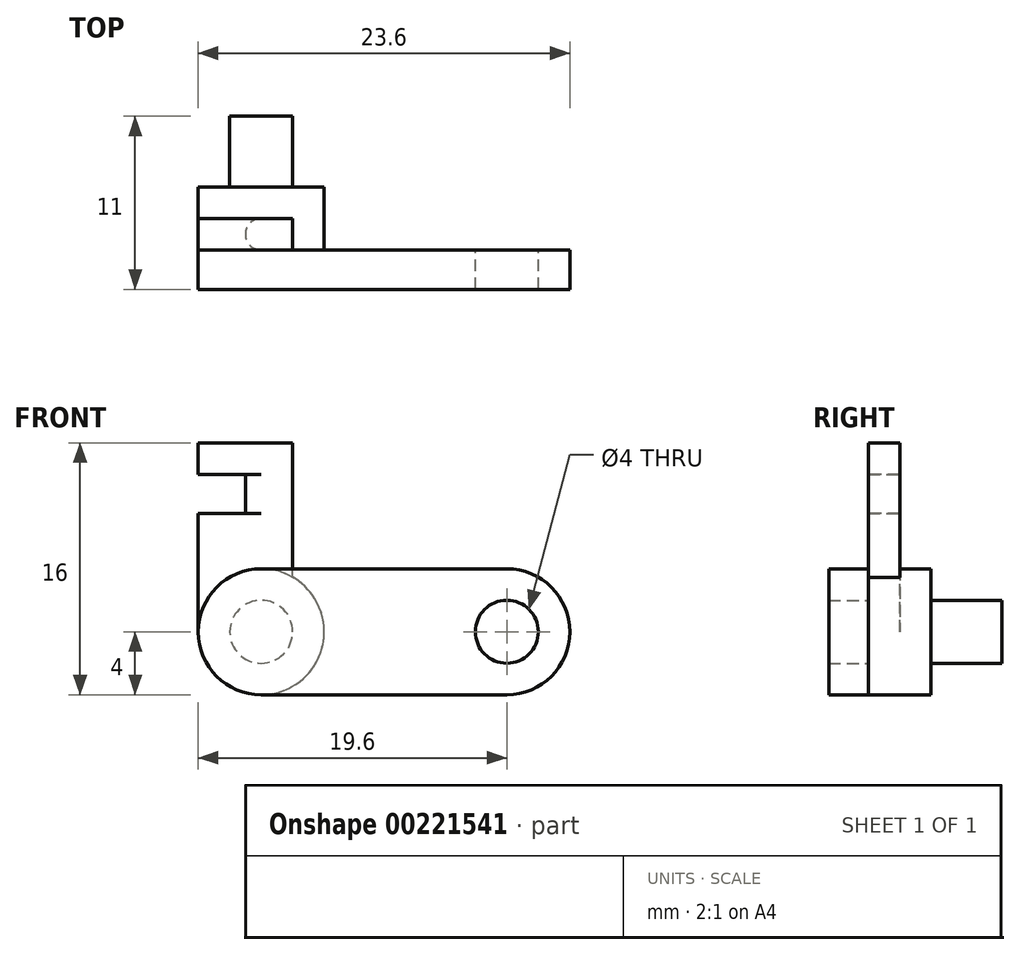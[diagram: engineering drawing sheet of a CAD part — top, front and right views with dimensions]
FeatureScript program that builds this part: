
annotation { "Feature Type Name" : "Feature", "Feature Type Description" : "" }
export const myFeature = defineFeature(function(context is Context, id is Id, definition is map)
    precondition{}
    {
        {
            var Q0;
            Q0=qCreatedBy(makeId("Front.planeOp"),FACE);
            var sketch = newSketch(context, id + "F0", { "sketchPlane" : qUnion([Q0])});
            skCircle(sketch, "E0", {"center": v(0, 0) * mm, "radius": 2 * mm});
            skCircle(sketch, "E1", {"center": v(0, 0) * mm, "radius": 4 * mm});
            skLineSegment(sketch, "E2", {"start": v(0, 4) * mm, "end": v(15.6, 4) * mm});
            skLineSegment(sketch, "E3", {"start": v(0, -4) * mm, "end": v(15.6, -4) * mm});
            skArc(sketch, "E4", {"start": v(15.6, 4) * mm, "mid": v(19.6, 0) * mm, "end": v(15.6, -4) * mm});
            skCircle(sketch, "E5", {"center": v(15.6, 0) * mm, "radius": 2 * mm});
            skLineSegment(sketch, "E6.bottom", {"start": v(2, 0) * mm, "end": v(-4, 0) * mm});
            skLineSegment(sketch, "E6.top", {"start": v(2, 12) * mm, "end": v(-4, 12) * mm});
            skLineSegment(sketch, "E6.left", {"start": v(2, 0) * mm, "end": v(2, 12) * mm});
            skLineSegment(sketch, "E6.right", {"start": v(-4, 0) * mm, "end": v(-4, 12) * mm});
            skLineSegment(sketch, "E7.bottom", {"start": v(-4, 10) * mm, "end": v(-1, 10) * mm});
            skLineSegment(sketch, "E7.top", {"start": v(-4, 7.5) * mm, "end": v(-1, 7.5) * mm});
            skLineSegment(sketch, "E7.left", {"start": v(-4, 10) * mm, "end": v(-4, 7.5) * mm});
            skLineSegment(sketch, "E7.right", {"start": v(-1, 10) * mm, "end": v(-1, 7.5) * mm});
            skSolve(sketch);
        }
        {
            var Q0;
            {var subQ1=sQuery(id+"F0.wireOp",EDGE,"E1");var subQ5=makeQuery(id+"F0.imprint","INTERSECT",VERTEX,{"derivedFrom":[subQ1,sQuery(id+"F0.wireOp",EDGE,"E3")]});Q0=makeQuery(id+"F0.imprint","IMPRINT",FACE,{"disambiguationData":[TD([[makeQuery(id+"F0.imprint","IMPRINT",EDGE,{"disambiguationData":[TD([[subQ5,-1.0]])],"derivedFrom":subQ1}),1.0]])]});}
            var Q1;
            {var subQ0=sQuery(id+"F0.wireOp",EDGE,"E2");var subQ1=sQuery(id+"F0.wireOp",EDGE,"E1");var subQ2=makeQuery(id+"F0.imprint","INTERSECT",VERTEX,{"derivedFrom":[subQ1,subQ0]});Q1=makeQuery(id+"F0.imprint","IMPRINT",FACE,{"disambiguationData":[TD([[makeQuery(id+"F0.imprint","IMPRINT",EDGE,{"disambiguationData":[TD([[subQ2,1.0]])],"derivedFrom":subQ1}),-1.0]])]});}
            var Q2;
            {var subQ1=sQuery(id+"F0.wireOp",EDGE,"E3");Q2=makeQuery(id+"F0.imprint","IMPRINT",FACE,{"disambiguationData":[TD([[makeQuery(id+"F0.imprint","IMPRINT",EDGE,{"derivedFrom":subQ1}),1.0]])]});}
            var Q3;
            {var subQ1=sQuery(id+"F0.wireOp",EDGE,"E1");var subQ5=makeQuery(id+"F0.imprint","INTERSECT",VERTEX,{"derivedFrom":[subQ1,sQuery(id+"F0.wireOp",EDGE,"E2")]});Q3=makeQuery(id+"F0.imprint","IMPRINT",FACE,{"disambiguationData":[TD([[makeQuery(id+"F0.imprint","IMPRINT",EDGE,{"disambiguationData":[TD([[subQ5,1.0]])],"derivedFrom":subQ1}),1.0]])]});}
            var Q4;
            {var subQ0=sQuery(id+"F0.wireOp",EDGE,"E6.bottom");var subQ1=sQuery(id+"F0.wireOp",EDGE,"E0");var subQ3=makeQuery(id+"F0.imprint","INTERSECT",VERTEX,{"derivedFrom":[subQ1,subQ0]});Q4=makeQuery(id+"F0.imprint","IMPRINT",FACE,{"disambiguationData":[TD([[makeQuery(id+"F0.imprint","IMPRINT",EDGE,{"disambiguationData":[TD([[subQ3,1.0]])],"derivedFrom":subQ1}),1.0]])]});}
            var Q5;
            {var subQ0=sQuery(id+"F0.wireOp",EDGE,"E6.bottom");var subQ1=sQuery(id+"F0.wireOp",EDGE,"E0");var subQ3=makeQuery(id+"F0.imprint","INTERSECT",VERTEX,{"derivedFrom":[subQ1,subQ0]});Q5=makeQuery(id+"F0.imprint","IMPRINT",FACE,{"disambiguationData":[TD([[makeQuery(id+"F0.imprint","IMPRINT",EDGE,{"disambiguationData":[TD([[subQ3,-1.0]])],"derivedFrom":subQ1}),1.0]])]});}
            extrude(context, id + "F1", {"entities" : qUnion([Q0, Q1, Q2, Q3, Q4, Q5]), "depth" : 2.5 * mm});
        }
        {
            var Q0;
            {var subQ1=sQuery(id+"F0.wireOp",EDGE,"E1");var subQ5=makeQuery(id+"F0.imprint","INTERSECT",VERTEX,{"derivedFrom":[subQ1,sQuery(id+"F0.wireOp",EDGE,"E2")]});Q0=makeQuery(id+"F0.imprint","IMPRINT",FACE,{"disambiguationData":[TD([[makeQuery(id+"F0.imprint","IMPRINT",EDGE,{"disambiguationData":[TD([[subQ5,1.0]])],"derivedFrom":subQ1}),1.0]])]});}
            var Q1;
            {var subQ1=sQuery(id+"F0.wireOp",EDGE,"E1");var subQ5=makeQuery(id+"F0.imprint","INTERSECT",VERTEX,{"derivedFrom":[subQ1,sQuery(id+"F0.wireOp",EDGE,"E3")]});Q1=makeQuery(id+"F0.imprint","IMPRINT",FACE,{"disambiguationData":[TD([[makeQuery(id+"F0.imprint","IMPRINT",EDGE,{"disambiguationData":[TD([[subQ5,-1.0]])],"derivedFrom":subQ1}),1.0]])]});}
            extrude(context, id + "F2", {"entities" : qUnion([Q0, Q1]), "operationType" : NewBodyOperationType.ADD, "oppositeDirection" : true, "depth" : 4 * mm});
        }
        {
            var Q0;
            {var subQ0=sQuery(id+"F0.wireOp",EDGE,"E6.bottom");var subQ1=sQuery(id+"F0.wireOp",EDGE,"E0");var subQ3=makeQuery(id+"F0.imprint","INTERSECT",VERTEX,{"derivedFrom":[subQ1,subQ0]});Q0=makeQuery(id+"F0.imprint","IMPRINT",FACE,{"disambiguationData":[TD([[makeQuery(id+"F0.imprint","IMPRINT",EDGE,{"disambiguationData":[TD([[subQ3,1.0]])],"derivedFrom":subQ1}),1.0]])]});}
            var Q1;
            {var subQ0=sQuery(id+"F0.wireOp",EDGE,"E6.bottom");var subQ1=sQuery(id+"F0.wireOp",EDGE,"E0");var subQ3=makeQuery(id+"F0.imprint","INTERSECT",VERTEX,{"derivedFrom":[subQ1,subQ0]});Q1=makeQuery(id+"F0.imprint","IMPRINT",FACE,{"disambiguationData":[TD([[makeQuery(id+"F0.imprint","IMPRINT",EDGE,{"disambiguationData":[TD([[subQ3,-1.0]])],"derivedFrom":subQ1}),1.0]])]});}
            extrude(context, id + "F3", {"entities" : qUnion([Q0, Q1]), "operationType" : NewBodyOperationType.ADD, "oppositeDirection" : true, "depth" : 8.5 * mm});
        }
        {
            var Q0;
            {var subQ0=sQuery(id+"F0.wireOp",EDGE,"E6.top");Q0=makeQuery(id+"F0.imprint","IMPRINT",FACE,{"disambiguationData":[TD([[makeQuery(id+"F0.imprint","IMPRINT",EDGE,{"derivedFrom":subQ0}),1.0]])]});}
            var Q1;
            {var subQ0=sQuery(id+"F0.wireOp",EDGE,"E2");var subQ1=sQuery(id+"F0.wireOp",EDGE,"E1");var subQ2=makeQuery(id+"F0.imprint","INTERSECT",VERTEX,{"derivedFrom":[subQ1,subQ0]});Q1=makeQuery(id+"F0.imprint","IMPRINT",FACE,{"disambiguationData":[TD([[makeQuery(id+"F0.imprint","IMPRINT",EDGE,{"disambiguationData":[TD([[subQ2,1.0]])],"derivedFrom":subQ1}),-1.0]])]});}
            var Q2;
            {var subQ1=sQuery(id+"F0.wireOp",EDGE,"E1");var subQ5=makeQuery(id+"F0.imprint","INTERSECT",VERTEX,{"derivedFrom":[subQ1,sQuery(id+"F0.wireOp",EDGE,"E2")]});Q2=makeQuery(id+"F0.imprint","IMPRINT",FACE,{"disambiguationData":[TD([[makeQuery(id+"F0.imprint","IMPRINT",EDGE,{"disambiguationData":[TD([[subQ5,1.0]])],"derivedFrom":subQ1}),1.0]])]});}
            var Q3;
            {var subQ0=sQuery(id+"F0.wireOp",EDGE,"E6.bottom");var subQ1=sQuery(id+"F0.wireOp",EDGE,"E0");var subQ3=makeQuery(id+"F0.imprint","INTERSECT",VERTEX,{"derivedFrom":[subQ1,subQ0]});Q3=makeQuery(id+"F0.imprint","IMPRINT",FACE,{"disambiguationData":[TD([[makeQuery(id+"F0.imprint","IMPRINT",EDGE,{"disambiguationData":[TD([[subQ3,1.0]])],"derivedFrom":subQ1}),1.0]])]});}
            var Q4;
            {var subQ0=sQuery(id+"F0.wireOp",EDGE,"E6.bottom");var subQ1=sQuery(id+"F0.wireOp",EDGE,"E0");var subQ3=makeQuery(id+"F0.imprint","INTERSECT",VERTEX,{"derivedFrom":[subQ1,subQ0]});Q4=makeQuery(id+"F0.imprint","IMPRINT",FACE,{"disambiguationData":[TD([[makeQuery(id+"F0.imprint","IMPRINT",EDGE,{"disambiguationData":[TD([[subQ3,-1.0]])],"derivedFrom":subQ1}),1.0]])]});}
            var Q5;
            {var subQ1=sQuery(id+"F0.wireOp",EDGE,"E1");var subQ5=makeQuery(id+"F0.imprint","INTERSECT",VERTEX,{"derivedFrom":[subQ1,sQuery(id+"F0.wireOp",EDGE,"E3")]});Q5=makeQuery(id+"F0.imprint","IMPRINT",FACE,{"disambiguationData":[TD([[makeQuery(id+"F0.imprint","IMPRINT",EDGE,{"disambiguationData":[TD([[subQ5,-1.0]])],"derivedFrom":subQ1}),1.0]])]});}
            extrude(context, id + "F4", {"entities" : qUnion([Q0, Q1, Q2, Q3, Q4, Q5]), "operationType" : NewBodyOperationType.ADD, "oppositeDirection" : true, "depth" : 2 * mm});
        }
        {
            var Q0;
            Q0=makeQuery(id+"F4.opExtrude","CAP_EDGE",EDGE,{"disambiguationData":[OSD([sQuery(id+"F0.wireOp",EDGE,"E7.right")])],"isStart":true});
            var Q1;
            Q1=makeQuery(id+"F4.opExtrude","CAP_EDGE",EDGE,{"disambiguationData":[OSD([sQuery(id+"F0.wireOp",EDGE,"E7.right")])],"isStart":false});
            fillet(context, id + "F5", {"entities" : qUnion([Q0, Q1]), "radius" : 1 * mm, "tangentPropagation" : true, "allowEdgeOverflow" : false});
        }
    });
